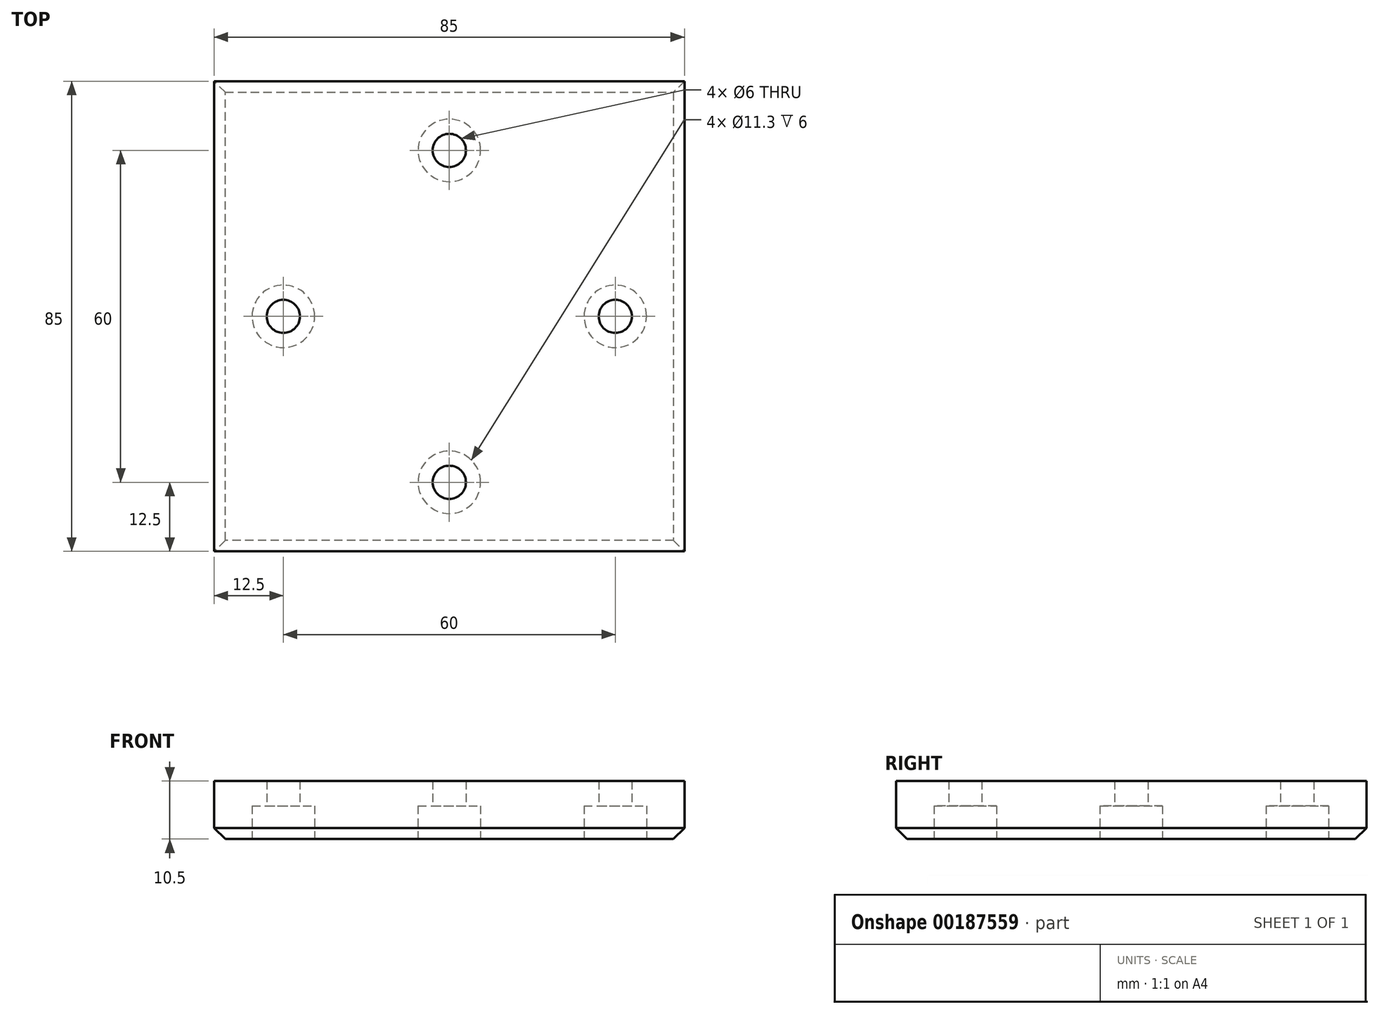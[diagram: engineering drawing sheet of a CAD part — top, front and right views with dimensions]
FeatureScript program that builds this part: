
annotation { "Feature Type Name" : "Feature", "Feature Type Description" : "" }
export const myFeature = defineFeature(function(context is Context, id is Id, definition is map)
    precondition{}
    {
        {
            var Q0;
            Q0=qCreatedBy(makeId("Top.planeOp"),FACE);
            var sketch = newSketch(context, id + "F0", { "sketchPlane" : qUnion([Q0])});
            skLineSegment(sketch, "E0.bottom", {"start": v(42.5, 42.5) * mm, "end": v(-42.5, 42.5) * mm});
            skLineSegment(sketch, "E0.top", {"start": v(42.5, -42.5) * mm, "end": v(-42.5, -42.5) * mm});
            skLineSegment(sketch, "E0.left", {"start": v(42.5, 42.5) * mm, "end": v(42.5, -42.5) * mm});
            skLineSegment(sketch, "E0.right", {"start": v(-42.5, 42.5) * mm, "end": v(-42.5, -42.5) * mm});
            skPoint(sketch, "E0.middle", {"position": v(0, 0) * mm});
            skSolve(sketch);
        }
        {
            var Q0;
            Q0=makeQuery(id+"F0.imprint","IMPRINT",FACE,{"disambiguationData":[TD([[makeQuery(id+"F0.imprint","IMPRINT",EDGE,{"derivedFrom":sQuery(id+"F0.wireOp",EDGE,"E0.bottom")}),1.0]])]});
            extrude(context, id + "F1", {"entities" : qUnion([Q0]), "depth" : 10.5 * mm});
        }
        {
            var Q0;
            Q0=makeQuery(id+"F1.opExtrude","CAP_FACE",FACE,{"disambiguationData":[OSD([sQuery(id+"F0.wireOp",EDGE,"E0.bottom"),sQuery(id+"F0.wireOp",EDGE,"E0.top"),sQuery(id+"F0.wireOp",EDGE,"E0.left"),sQuery(id+"F0.wireOp",EDGE,"E0.right")])],"isStart":true});
            var sketch = newSketch(context, id + "F3", { "sketchPlane" : qUnion([Q0])});
            skLineSegment(sketch, "E1.0", {"start": v(-30, -30) * mm, "end": v(-30, 30) * mm, "construction": true});
            skLineSegment(sketch, "E2.0", {"start": v(30, 30) * mm, "end": v(-30, 30) * mm, "construction": true});
            skLineSegment(sketch, "E3.0", {"start": v(30, -30) * mm, "end": v(30, 30) * mm, "construction": true});
            skLineSegment(sketch, "E4.0", {"start": v(30, -30) * mm, "end": v(-30, -30) * mm, "construction": true});
            skLineSegment(sketch, "E5", {"start": v(-42.5, 0) * mm, "end": v(42.5, 0) * mm, "construction": true});
            skLineSegment(sketch, "E6", {"start": v(0, 42.5) * mm, "end": v(0, -42.5) * mm, "construction": true});
            skLineSegment(sketch, "E7", {"start": v(30, 3.5) * mm, "end": v(30, -3.5) * mm, "construction": true});
            skArc(sketch, "E8.0.startCap", {"start": v(25, 3.5) * mm, "mid": v(30, 8.5) * mm, "end": v(35, 3.5) * mm});
            skArc(sketch, "E8.0.endCap", {"start": v(35, -3.5) * mm, "mid": v(30, -8.5) * mm, "end": v(25, -3.5) * mm});
            skLineSegment(sketch, "E8.0.left", {"start": v(35, 3.5) * mm, "end": v(35, -3.5) * mm});
            skLineSegment(sketch, "E8.0.right", {"start": v(25, 3.5) * mm, "end": v(25, -3.5) * mm});
            skPoint(sketch, "E9", {"position": v(30, 0) * mm});
            skLineSegment(sketch, "E10", {"start": v(3.5, 30) * mm, "end": v(-3.5, 30) * mm, "construction": true});
            skArc(sketch, "E11.0.startCap", {"start": v(3.5, 35) * mm, "mid": v(8.5, 30) * mm, "end": v(3.5, 25) * mm});
            skArc(sketch, "E11.0.endCap", {"start": v(-3.5, 25) * mm, "mid": v(-8.5, 30) * mm, "end": v(-3.5, 35) * mm});
            skLineSegment(sketch, "E11.0.left", {"start": v(3.5, 25) * mm, "end": v(-3.5, 25) * mm});
            skLineSegment(sketch, "E11.0.right", {"start": v(3.5, 35) * mm, "end": v(-3.5, 35) * mm});
            skArc(sketch, "E12.MirrorCS", {"start": v(35, 3.5) * mm, "mid": v(30, 8.5) * mm, "end": v(25, 3.5) * mm});
            skArc(sketch, "E13.MirrorCS", {"start": v(25, -3.5) * mm, "mid": v(30, -8.5) * mm, "end": v(35, -3.5) * mm});
            skPoint(sketch, "E14.MirrorP", {"position": v(-30, 0) * mm});
            skArc(sketch, "E15.MirrorCS", {"start": v(-35, 3.5) * mm, "mid": v(-30, 8.5) * mm, "end": v(-25, 3.5) * mm});
            skArc(sketch, "E16.MirrorCS", {"start": v(-35, -3.5) * mm, "mid": v(-30, -8.5) * mm, "end": v(-25, -3.5) * mm});
            skLineSegment(sketch, "E17.MirrorCS", {"start": v(-35, 3.5) * mm, "end": v(-35, -3.5) * mm});
            skLineSegment(sketch, "E18.MirrorCS", {"start": v(-25, 3.5) * mm, "end": v(-25, -3.5) * mm});
            skArc(sketch, "E19.MirrorCS", {"start": v(-25, 3.5) * mm, "mid": v(-30, 8.5) * mm, "end": v(-35, 3.5) * mm});
            skLineSegment(sketch, "E20.MirrorCS", {"start": v(-30, 3.5) * mm, "end": v(-30, -3.5) * mm, "construction": true});
            skArc(sketch, "E21.MirrorCS", {"start": v(-25, -3.5) * mm, "mid": v(-30, -8.5) * mm, "end": v(-35, -3.5) * mm});
            skPoint(sketch, "E22", {"position": v(0, 30) * mm});
            skLineSegment(sketch, "E23.MirrorCS", {"start": v(3.5, -35) * mm, "end": v(-3.5, -35) * mm});
            skLineSegment(sketch, "E24.MirrorCS", {"start": v(3.5, -30) * mm, "end": v(-3.5, -30) * mm, "construction": true});
            skLineSegment(sketch, "E25.MirrorCS", {"start": v(3.5, -25) * mm, "end": v(-3.5, -25) * mm});
            skPoint(sketch, "E26.MirrorP", {"position": v(0, -30) * mm});
            skArc(sketch, "E27.MirrorCS", {"start": v(-3.5, -25) * mm, "mid": v(-8.5, -30) * mm, "end": v(-3.5, -35) * mm});
            skArc(sketch, "E28.MirrorCS", {"start": v(3.5, -35) * mm, "mid": v(8.5, -30) * mm, "end": v(3.5, -25) * mm});
            skSolve(sketch);
        }
        {
            var Q0;
            Q0=makeQuery(id+"F1.opExtrude","CAP_FACE",FACE,{"disambiguationData":[OSD([sQuery(id+"F0.wireOp",EDGE,"E0.bottom"),sQuery(id+"F0.wireOp",EDGE,"E0.top"),sQuery(id+"F0.wireOp",EDGE,"E0.left"),sQuery(id+"F0.wireOp",EDGE,"E0.right")])],"isStart":true});
            var sketch = newSketch(context, id + "F4", { "sketchPlane" : qUnion([Q0])});
            skCircle(sketch, "E29", {"center": v(0, 30) * mm, "radius": 3 * mm});
            skPoint(sketch, "E29.centerSnap0", {"position": v(0, 35) * mm});
            skPoint(sketch, "E29.centerSnap1", {"position": v(8.5, 30) * mm});
            skCircle(sketch, "E30.MirrorC", {"center": v(0, -30) * mm, "radius": 3 * mm});
            skCircle(sketch, "E31", {"center": v(30, 0) * mm, "radius": 3 * mm});
            skPoint(sketch, "E31.centerSnap0", {"position": v(30, 8.5) * mm});
            skCircle(sketch, "E32.MirrorC", {"center": v(-30, 0) * mm, "radius": 3 * mm});
            skSolve(sketch);
        }
        {
            var Q0;
            Q0=qSketchRegion(id+"F4",true);
            extrude(context, id + "F5", {"entities" : qUnion([Q0]), "operationType" : NewBodyOperationType.REMOVE, "oppositeDirection" : true, "depth" : 25 * mm});
        }
        {
            var Q0;
            Q0=makeQuery(id+"F1.opExtrude","CAP_FACE",FACE,{"disambiguationData":[OSD([sQuery(id+"F0.wireOp",EDGE,"E0.bottom"),sQuery(id+"F0.wireOp",EDGE,"E0.top"),sQuery(id+"F0.wireOp",EDGE,"E0.left"),sQuery(id+"F0.wireOp",EDGE,"E0.right")])],"isStart":true});
            var sketch = newSketch(context, id + "F6", { "sketchPlane" : qUnion([Q0])});
            skCircle(sketch, "E33.0", {"center": v(-30, 0) * mm, "radius": 3 * mm});
            skCircle(sketch, "E34.0", {"center": v(0, 30) * mm, "radius": 3 * mm});
            skCircle(sketch, "E35.0", {"center": v(30, 0) * mm, "radius": 3 * mm});
            skCircle(sketch, "E36.0", {"center": v(0, -30) * mm, "radius": 3 * mm});
            skCircle(sketch, "E37", {"center": v(0, 30) * mm, "radius": 5.65 * mm});
            skCircle(sketch, "E38", {"center": v(30, 0) * mm, "radius": 5.65 * mm});
            skCircle(sketch, "E39", {"center": v(0, -30) * mm, "radius": 5.65 * mm});
            skCircle(sketch, "E40", {"center": v(-30, 0) * mm, "radius": 5.65 * mm});
            skSolve(sketch);
        }
        {
            var Q0;
            Q0 = qSketchRegion(id + "F6", true);
            extrude(context, id + "F7", {"entities" : qUnion([Q0]), "operationType" : NewBodyOperationType.REMOVE, "oppositeDirection" : true, "depth" : 6 * mm});
        }
        {
            var Q0;
            Q0=makeQuery(id+"F1.opExtrude","CAP_EDGE",EDGE,{"disambiguationData":[OSD([sQuery(id+"F0.wireOp",EDGE,"E0.right")])],"isStart":true});
            var Q1;
            Q1=makeQuery(id+"F1.opExtrude","CAP_EDGE",EDGE,{"disambiguationData":[OSD([sQuery(id+"F0.wireOp",EDGE,"E0.top")])],"isStart":true});
            var Q2;
            Q2=makeQuery(id+"F1.opExtrude","CAP_EDGE",EDGE,{"disambiguationData":[OSD([sQuery(id+"F0.wireOp",EDGE,"E0.left")])],"isStart":true});
            var Q3;
            Q3=makeQuery(id+"F1.opExtrude","CAP_EDGE",EDGE,{"disambiguationData":[OSD([sQuery(id+"F0.wireOp",EDGE,"E0.bottom")])],"isStart":true});
            chamfer(context, id + "F8", {"entities" : qUnion([Q0, Q1, Q2, Q3]), "width" : 2 * mm, "tangentPropagation" : true});
        }
    });
